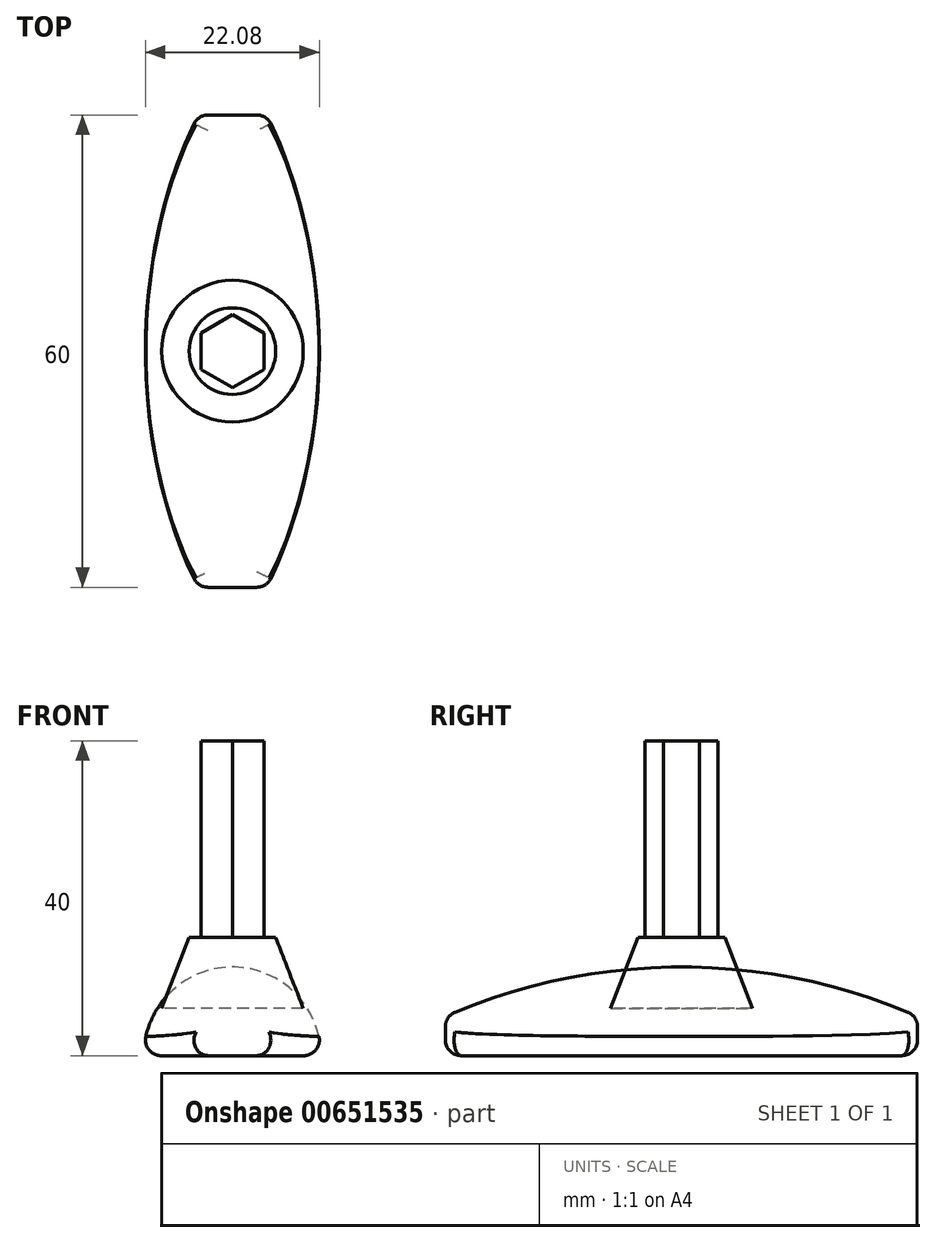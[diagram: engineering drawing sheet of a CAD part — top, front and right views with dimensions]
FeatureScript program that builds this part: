
annotation { "Feature Type Name" : "Feature", "Feature Type Description" : "" }
export const myFeature = defineFeature(function(context is Context, id is Id, definition is map)
    precondition{}
    {
        {
            var Q0;
            Q0=qCreatedBy(makeId("Top.planeOp"),FACE);
            cPlane(context, id + "F0", {"entities" : qUnion([Q0]), "cplaneType" : CPlaneType.OFFSET, "offset" : 15 * mm, "oppositeDirection" : true, "width" : 150 * mm, "height" : 150 * mm});
        }
        {
            var Q0;
            Q0=qCreatedBy(makeId("Top.planeOp"),FACE);
            var sketch = newSketch(context, id + "F1", { "sketchPlane" : qUnion([Q0])});
            skCircle(sketch, "E0.cCircle", {"center": v(0, 0) * mm, "radius": 4 * mm, "construction": true});
            skLineSegment(sketch, "E0.0", {"start": v(-4, 2.3) * mm, "end": v(0, 4.62) * mm});
            skLineSegment(sketch, "E0.1", {"start": v(0, 4.62) * mm, "end": v(4, 2.3) * mm});
            skLineSegment(sketch, "E0.2", {"start": v(4, 2.3) * mm, "end": v(4, -2.3) * mm});
            skLineSegment(sketch, "E0.3", {"start": v(4, -2.3) * mm, "end": v(0, -4.62) * mm});
            skLineSegment(sketch, "E0.4", {"start": v(0, -4.62) * mm, "end": v(-4, -2.3) * mm});
            skLineSegment(sketch, "E0.5", {"start": v(-4, -2.3) * mm, "end": v(-4, 2.3) * mm});
            skPoint(sketch, "E0.0.midPoint", {"position": v(-2, 3.46) * mm});
            skSolve(sketch);
        }
        {
            var Q0;
            Q0 = qSketchRegion(id + "F1", true);
            extrude(context, id + "F2", {"entities" : qUnion([Q0]), "depth" : 25 * mm, "offsetDistance" : 25 * mm});
        }
        {
            var Q0;
            Q0=qCreatedBy(makeId("Right.planeOp"),FACE);
            var sketch = newSketch(context, id + "F3", { "sketchPlane" : qUnion([Q0])});
            skLineSegment(sketch, "E1", {"start": v(0, 0) * mm, "end": v(5.5, 0) * mm});
            skLineSegment(sketch, "E2", {"start": v(5.5, 0) * mm, "end": v(9, -9) * mm});
            skLineSegment(sketch, "E3", {"start": v(9, -9) * mm, "end": v(0, -9) * mm});
            skLineSegment(sketch, "E4", {"start": v(0, 0) * mm, "end": v(0, -9) * mm});
            skLineSegment(sketch, "E5", {"start": v(0, 2.85) * mm, "end": v(0, -11.78) * mm, "construction": true});
            skSolve(sketch);
        }
        {
            var Q0;
            Q0=makeQuery(id+"F3.imprint","IMPRINT",FACE,{"disambiguationData":[TD([[makeQuery(id+"F3.imprint","IMPRINT",EDGE,{"derivedFrom":sQuery(id+"F3.wireOp",EDGE,"E1")}),-1.0]])]});
            var Q1;
            Q1 = qSketchRegion(id + "F5", true);
            var Q2;
            Q2=sQuery(id+"F3.wireOp",EDGE,"E4");
            revolve(context, id + "F4", {"surfaceOperationType" : NewSurfaceOperationType.NEW, "entities" : qUnion([Q0, Q1]), "axis" : qUnion([Q2]), "revolveType" : RevolveType.FULL});
        }
        {
            var Q0;
            Q0=qCreatedBy(id+"F0.planeOp",FACE);
            var sketch = newSketch(context, id + "F5", { "sketchPlane" : qUnion([Q0])});
            skLineSegment(sketch, "E6", {"start": v(0, 30) * mm, "end": v(0, -30) * mm});
            skLineSegment(sketch, "E7", {"start": v(0, -30) * mm, "end": v(5, -30) * mm});
            skLineSegment(sketch, "E8", {"start": v(0, 30) * mm, "end": v(5, 30) * mm});
            skArc(sketch, "E9", {"start": v(5, -30) * mm, "mid": v(11.26, 0) * mm, "end": v(5, 30) * mm});
            skLineSegment(sketch, "E10", {"start": v(0, -43.97) * mm, "end": v(0, 40.8) * mm, "construction": true});
            skSolve(sketch);
        }
        {
            var Q0;
            Q0=makeQuery(id+"F5.imprint","IMPRINT",FACE,{"disambiguationData":[TD([[makeQuery(id+"F5.imprint","IMPRINT",EDGE,{"derivedFrom":sQuery(id+"F5.wireOp",EDGE,"E6")}),1.0]])]});
            var Q1;
            Q1=sQuery(id+"F5.wireOp",EDGE,"E10");
            revolve(context, id + "F6", {"entities" : qUnion([Q0]), "axis" : qUnion([Q1]), "revolveType" : RevolveType.ONE_DIRECTION, "oppositeDirection" : true, "angle" : 180 * degree});
        }
        {
            var Q0;
            Q0=makeQuery(id+"F6.opRevolve","CAP_EDGE",EDGE,{"disambiguationData":[OSD([sQuery(id+"F5.wireOp",EDGE,"E9")])],"isStart":true});
            var Q1;
            Q1=makeQuery(id+"F6.opRevolve","CAP_EDGE",EDGE,{"disambiguationData":[OSD([sQuery(id+"F5.wireOp",EDGE,"E9")])],"isStart":false});
            var Q2;
            Q2=makeQuery(id+"F6.opRevolve","CAP_EDGE",EDGE,{"disambiguationData":[OSD([sQuery(id+"F5.wireOp",EDGE,"E7")])],"isStart":false});
            var Q3;
            Q3=makeQuery(id+"F6.opRevolve","CAP_EDGE",EDGE,{"disambiguationData":[OSD([sQuery(id+"F5.wireOp",EDGE,"E8")])],"isStart":false});
            var Q4;
            Q4=makeQuery(id+"F6.opRevolve","SWEPT_EDGE",EDGE,{"disambiguationData":[OSD([sQuery(id+"F5.wireOp",EDGE,"E8"),sQuery(id+"F5.wireOp",EDGE,"E9")])]});
            var Q5;
            Q5=makeQuery(id+"F6.opRevolve","SWEPT_EDGE",EDGE,{"disambiguationData":[OSD([sQuery(id+"F5.wireOp",EDGE,"E7"),sQuery(id+"F5.wireOp",EDGE,"E9")])]});
            fillet(context, id + "F7", {"entities" : qUnion([Q0, Q1, Q2, Q3, Q4, Q5]), "radius" : 2 * mm, "tangentPropagation" : true, "defaultsChanged" : false, "vertexSettings" : [], "allowEdgeOverflow" : false});
        }
    });
